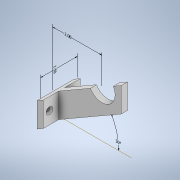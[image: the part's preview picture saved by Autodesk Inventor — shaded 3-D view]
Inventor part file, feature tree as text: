
AUTODESK INVENTOR PART (.ipt)
format: ipt  version: 2021.1 (Build 251245000, 245)  size: 164,864 bytes
history: native  units: in
note: dims shown in document units (in); Inventor stores cm internally (conversion verified against a paired STEP export)
features: sketch x5, other x4, extrude x4, hole x1
ambient origin geometry x8: Origin, YZ Plane, XZ Plane, XY Plane, X Axis, Y Axis, Z Axis, Center Point
bodies: Solid2 (feature_tree)
feature tree (14):
  other  "Annotations"
  extrude  "Extrusion3"  Depth=0.25in
  extrude  "Extrusion4"  TaperAngle=30.0deg  [1 undecoded]
  sketch  "Sketch7"  dims[d26=1.075in d29=0.25in]
  extrude  "Extrusion5"  Depth=0.25in
  hole  "Hole3"  [1 undecoded]
  extrude  "Extrusion6"  TaperAngle=0.0deg  [1 undecoded]
  sketch  "Sketch5"  dims[d21=1.0in d22=0.25in]
  sketch  "Sketch6"  dims[d23=1.5in d24=0.0in d25=30.0deg]
  sketch  "Sketch8"  dims[d30=2.0in d31=0.25in]
  sketch  "Sketch9"  dims[d32=0.0in d33=0.0in d34=0.25in d35=0.25in d47=1.5in d48=0.0in d49=0.15in d50=0.75in d51=0.279in d52=0.25in d53=0.5635in d54=1.0in d55=0.8108in d63=1.5in d64=0.0in d56=0.2085in d57=0.331in d58=1.5in d59=2.3174in d60=30.0deg d62=2.0in]
  other  "Linear Dimension 1"
  other  "Angular Dimension 1"
  other  "Linear Dimension 3"
note: 3 required parameter values undecoded (feature->parameter linkage not recoverable at this tier; creation-order binding heuristic only, values carry confidence <= 0.55)
